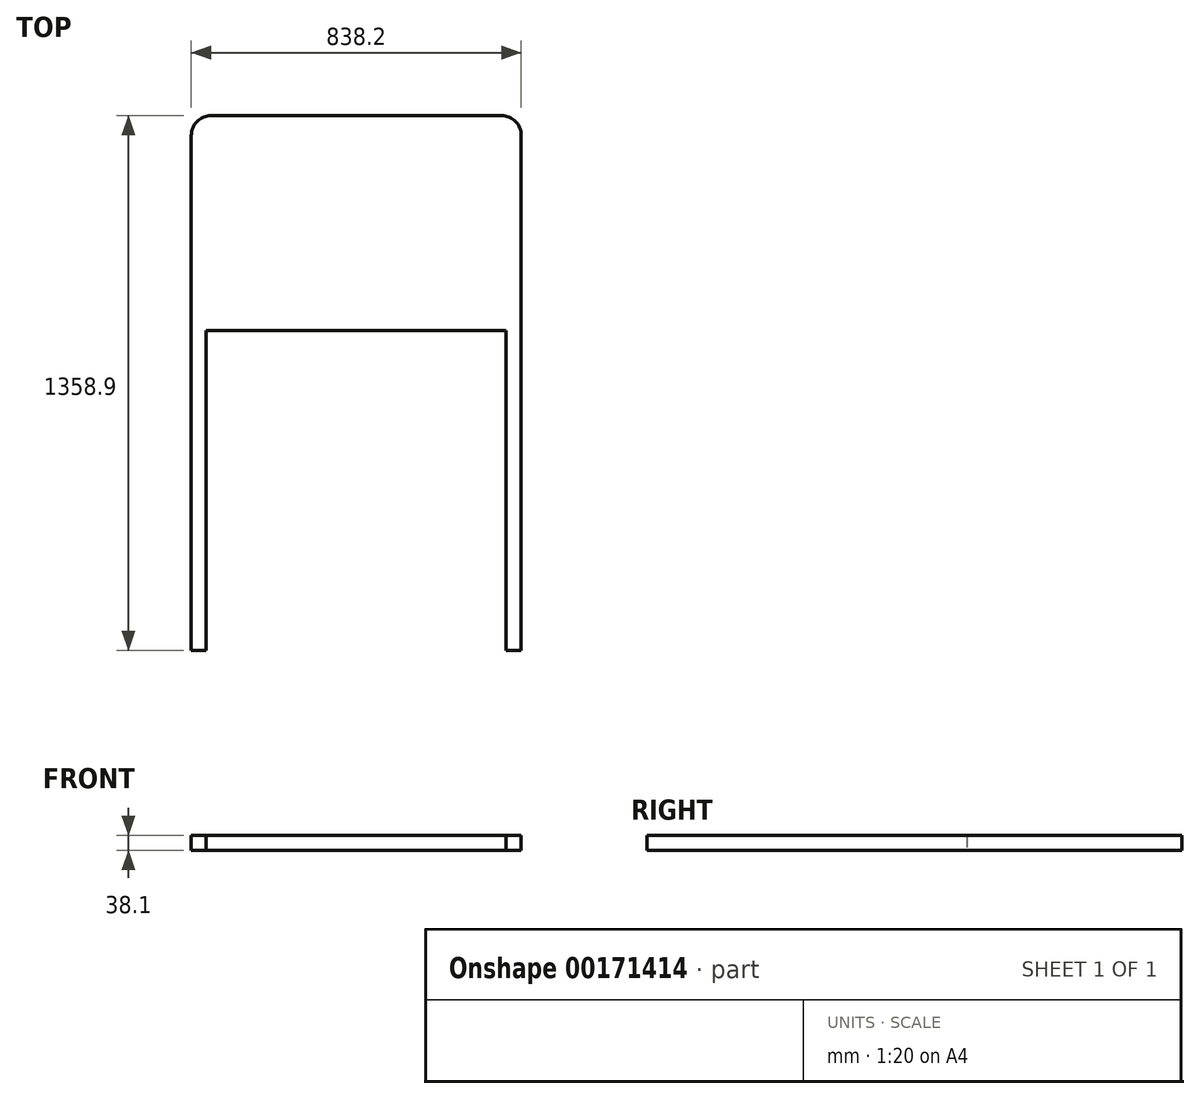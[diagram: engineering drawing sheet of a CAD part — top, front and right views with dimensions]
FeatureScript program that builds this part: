
annotation { "Feature Type Name" : "Feature", "Feature Type Description" : "" }
export const myFeature = defineFeature(function(context is Context, id is Id, definition is map)
    precondition{}
    {
        {
            var Q0;
            Q0=qCreatedBy(makeId("Top.planeOp"),FACE);
            var sketch = newSketch(context, id + "F0", { "sketchPlane" : qUnion([Q0])});
            skLineSegment(sketch, "E0.bottom", {"start": v(-368.3, 679.45) * mm, "end": v(368.3, 679.45) * mm});
            skLineSegment(sketch, "E0.top", {"start": v(-419.1, -679.45) * mm, "end": v(419.1, -679.45) * mm, "construction": true});
            skLineSegment(sketch, "E0.left", {"start": v(-419.1, 628.65) * mm, "end": v(-419.1, -679.45) * mm});
            skLineSegment(sketch, "E0.right", {"start": v(419.1, 628.65) * mm, "end": v(419.1, -679.45) * mm});
            skPoint(sketch, "E0.middle", {"position": v(0, 0) * mm});
            skLineSegment(sketch, "E1", {"start": v(-381, -679.45) * mm, "end": v(-381, 133.35) * mm});
            skLineSegment(sketch, "E2", {"start": v(-381, 133.35) * mm, "end": v(381, 133.35) * mm});
            skLineSegment(sketch, "E3", {"start": v(381, 133.35) * mm, "end": v(381, -679.45) * mm});
            skLineSegment(sketch, "E4", {"start": v(-419.1, -679.45) * mm, "end": v(-381, -679.45) * mm});
            skLineSegment(sketch, "E5", {"start": v(381, -679.45) * mm, "end": v(419.1, -679.45) * mm});
            skPoint(sketch, "E6.visualSharp", {"position": v(419.1, 679.45) * mm});
            skArc(sketch, "E6.filletArc", {"start": v(419.1, 628.65) * mm, "mid": v(404.22, 664.57) * mm, "end": v(368.3, 679.45) * mm});
            skPoint(sketch, "E7.visualSharp", {"position": v(-419.1, 679.45) * mm});
            skArc(sketch, "E7.filletArc", {"start": v(-368.3, 679.45) * mm, "mid": v(-404.22, 664.57) * mm, "end": v(-419.1, 628.65) * mm});
            skSolve(sketch);
        }
        {
            var Q0;
            Q0=makeQuery(id+"F0.imprint","IMPRINT",FACE,{"disambiguationData":[TD([[makeQuery(id+"F0.imprint","IMPRINT",EDGE,{"derivedFrom":sQuery(id+"F0.wireOp",EDGE,"E0.bottom")}),-1.0]])]});
            extrude(context, id + "F1", {"entities" : qUnion([Q0]), "depth" : 38.1 * mm});
        }
    });
